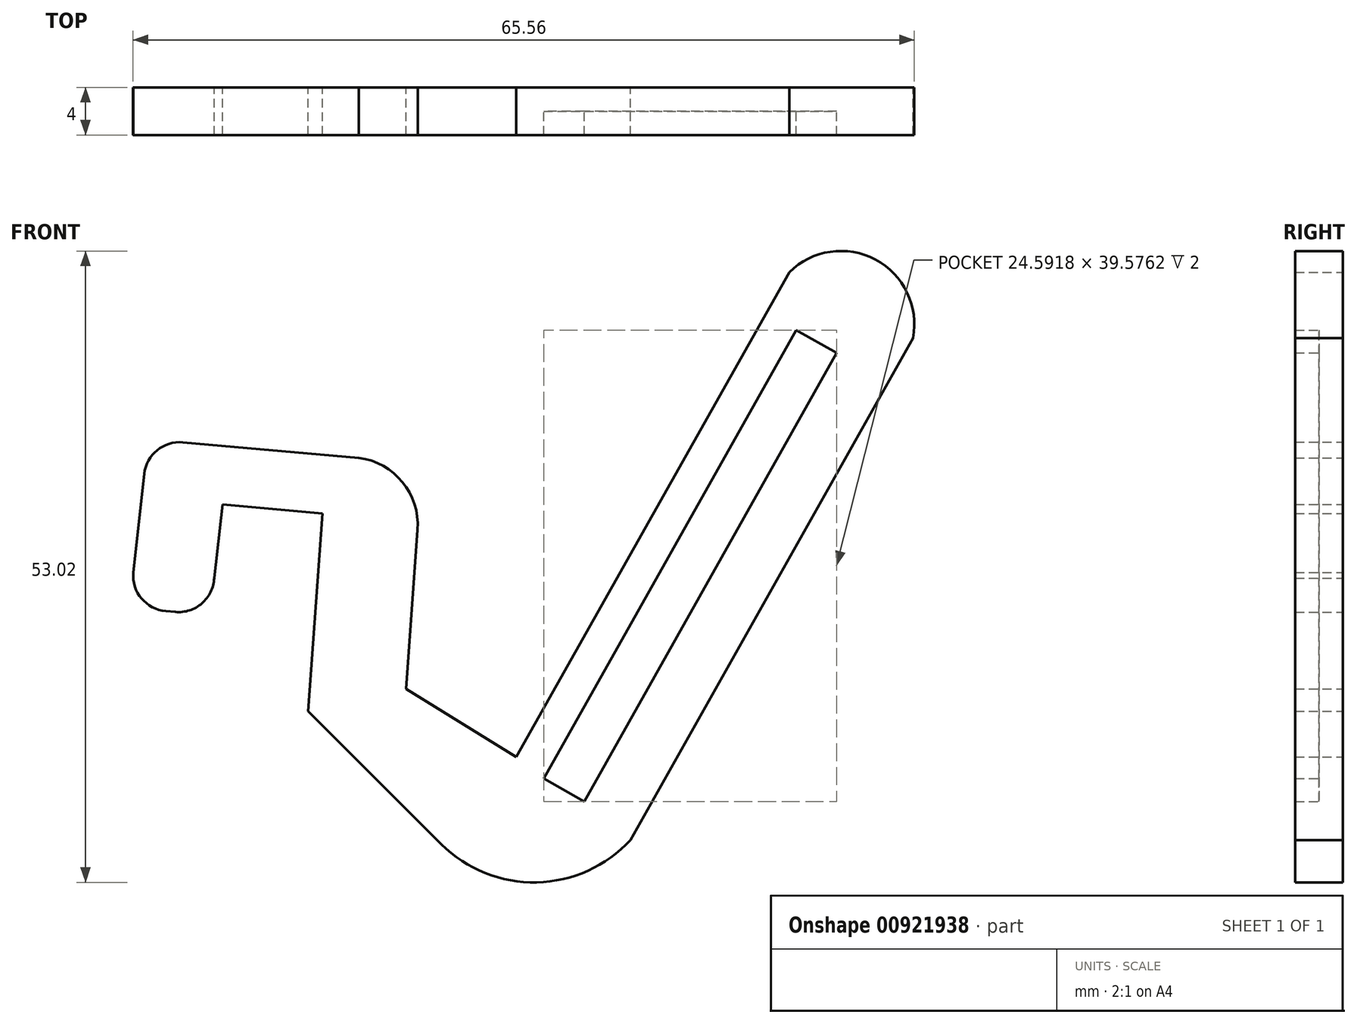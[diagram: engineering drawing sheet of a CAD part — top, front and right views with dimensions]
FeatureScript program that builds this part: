
annotation { "Feature Type Name" : "Feature", "Feature Type Description" : "" }
export const myFeature = defineFeature(function(context is Context, id is Id, definition is map)
    precondition{}
    {
        {
            var Q0;
            Q0=qCreatedBy(makeId("Front.planeOp"),FACE);
            var sketch = newSketch(context, id + "F0", { "sketchPlane" : qUnion([Q0])});
            skLineSegment(sketch, "E0", {"start": v(-66.3, 26.15) * mm, "end": v(-65.48, 26.08) * mm});
            skLineSegment(sketch, "E1", {"start": v(-31.17, 10.17) * mm, "end": v(-34.57, 12.08) * mm});
            skLineSegment(sketch, "E2", {"start": v(-34.57, 12.08) * mm, "end": v(-13.38, 49.74) * mm});
            skPoint(sketch, "E3.visualSharp", {"position": v(-10.27, 46.46) * mm});
            skPoint(sketch, "E4.visualSharp", {"position": v(-5.8, 46.46) * mm});
            skPoint(sketch, "E5.visualSharp", {"position": v(-54.33, 25.35) * mm});
            skArc(sketch, "E5.filletArc", {"start": v(-65.48, 26.08) * mm, "mid": v(-63.25, 26.8) * mm, "end": v(-62.23, 28.91) * mm});
            skPoint(sketch, "E6.visualSharp", {"position": v(-69.3, 26.15) * mm});
            skArc(sketch, "E6.filletArc", {"start": v(-69.02, 29.4) * mm, "mid": v(-68.33, 27.2) * mm, "end": v(-66.3, 26.15) * mm});
            skPoint(sketch, "E7.endSnap0", {"position": v(-55.65, 34.56) * mm});
            skPoint(sketch, "E8.visualSharp", {"position": v(-33.14, 38.58) * mm});
            skLineSegment(sketch, "E9", {"start": v(-3.57, 49.09) * mm, "end": v(-27.3, 6.93) * mm});
            skLineSegment(sketch, "E10", {"start": v(-34.47, 5.2) * mm, "end": v(-34.23, 4.71) * mm});
            skLineSegment(sketch, "E11", {"start": v(-13.38, 49.74) * mm, "end": v(-9.98, 47.83) * mm});
            skPoint(sketch, "E12.endSnap0", {"position": v(-3.2, 46.46) * mm});
            skArc(sketch, "E13.filletArc", {"start": v(-0.53, 46.59) * mm, "mid": v(-0.53, 46.6) * mm, "end": v(-0.53, 46.6) * mm});
            skLineSegment(sketch, "E14", {"start": v(-9.98, 47.83) * mm, "end": v(-31.17, 10.17) * mm});
            skPoint(sketch, "E15.visualSharp", {"position": v(-46.23, 38.9) * mm});
            skLineSegment(sketch, "E15.filletArc", {"start": v(-12.65, 38.15) * mm, "end": v(-12.65, 38.15) * mm});
            skLineSegment(sketch, "E16", {"start": v(-61.54, 35.1) * mm, "end": v(-62.23, 28.91) * mm});
            skLineSegment(sketch, "E17", {"start": v(-69.02, 29.4) * mm, "end": v(-68.1, 37.67) * mm});
            skLineSegment(sketch, "E18", {"start": v(-64.85, 40.32) * mm, "end": v(-50.08, 39.02) * mm});
            skLineSegment(sketch, "E19", {"start": v(-53.15, 34.36) * mm, "end": v(-61.54, 35.1) * mm});
            skPoint(sketch, "E20.visualSharp", {"position": v(-67.77, 40.58) * mm});
            skArc(sketch, "E20.filletArc", {"start": v(-64.85, 40.32) * mm, "mid": v(-67.01, 39.66) * mm, "end": v(-68.1, 37.67) * mm});
            skLineSegment(sketch, "E21", {"start": v(-53.15, 34.36) * mm, "end": v(-54.33, 17.73) * mm});
            skLineSegment(sketch, "E22", {"start": v(-54.33, 17.73) * mm, "end": v(-43.16, 6.58) * mm});
            skArc(sketch, "E23", {"start": v(-43.16, 6.58) * mm, "mid": v(-35.16, 3.37) * mm, "end": v(-27.3, 6.93) * mm});
            skLineSegment(sketch, "E24", {"start": v(-45.16, 33) * mm, "end": v(-46.11, 19.6) * mm});
            skLineSegment(sketch, "E25", {"start": v(-46.11, 19.6) * mm, "end": v(-36.88, 13.9) * mm});
            skLineSegment(sketch, "E26", {"start": v(-36.88, 13.9) * mm, "end": v(-13.96, 54.61) * mm});
            skArc(sketch, "E27", {"start": v(-3.57, 49.09) * mm, "mid": v(-6.74, 55.67) * mm, "end": v(-13.96, 54.61) * mm});
            skArc(sketch, "E28", {"start": v(-45.16, 33) * mm, "mid": v(-46.43, 36.99) * mm, "end": v(-50.08, 39.02) * mm});
            skArc(sketch, "E29.MirrorCS", {"start": v(2.14, 46.59) * mm, "mid": v(2.13, 46.6) * mm, "end": v(2.13, 46.6) * mm});
            skPoint(sketch, "E30.MirrorP", {"position": v(4.8, 46.46) * mm});
            skSolve(sketch);
        }
        {
            var Q0;
            Q0=makeQuery(id+"F0.imprint","IMPRINT",FACE,{"disambiguationData":[TD([[makeQuery(id+"F0.imprint","IMPRINT",EDGE,{"derivedFrom":sQuery(id+"F0.wireOp",EDGE,"E0")}),1.0]])]});
            var Q1;
            Q1=makeQuery(id+"F0.imprint","IMPRINT",FACE,{"disambiguationData":[TD([[makeQuery(id+"F0.imprint","IMPRINT",EDGE,{"derivedFrom":sQuery(id+"F0.wireOp",EDGE,"da98becc-92d7-4b94-83fd-4495f5c078e32.MirrorCS")}),-1.0]])]});
            extrude(context, id + "F1", {"entities" : qUnion([Q0, Q1]), "depth" : 4 * mm, "offsetDistance" : 25 * mm});
        }
        {
            var Q0;
            Q0=makeQuery(id+"F0.imprint","IMPRINT",FACE,{"disambiguationData":[TD([[makeQuery(id+"F0.imprint","IMPRINT",EDGE,{"derivedFrom":sQuery(id+"F0.wireOp",EDGE,"E1")}),-1.0]])]});
            var Q1;
            Q1=makeQuery(id+"F0.imprint","IMPRINT",FACE,{"disambiguationData":[TD([[makeQuery(id+"F0.imprint","IMPRINT",EDGE,{"derivedFrom":sQuery(id+"F0.wireOp",EDGE,"da98becc-92d7-4b94-83fd-4495f5c078e33.MirrorCS")}),1.0]])]});
            extrude(context, id + "F2", {"entities" : qUnion([Q0, Q1]), "operationType" : NewBodyOperationType.ADD, "depth" : 2 * mm, "offsetDistance" : 25 * mm});
        }
    });
